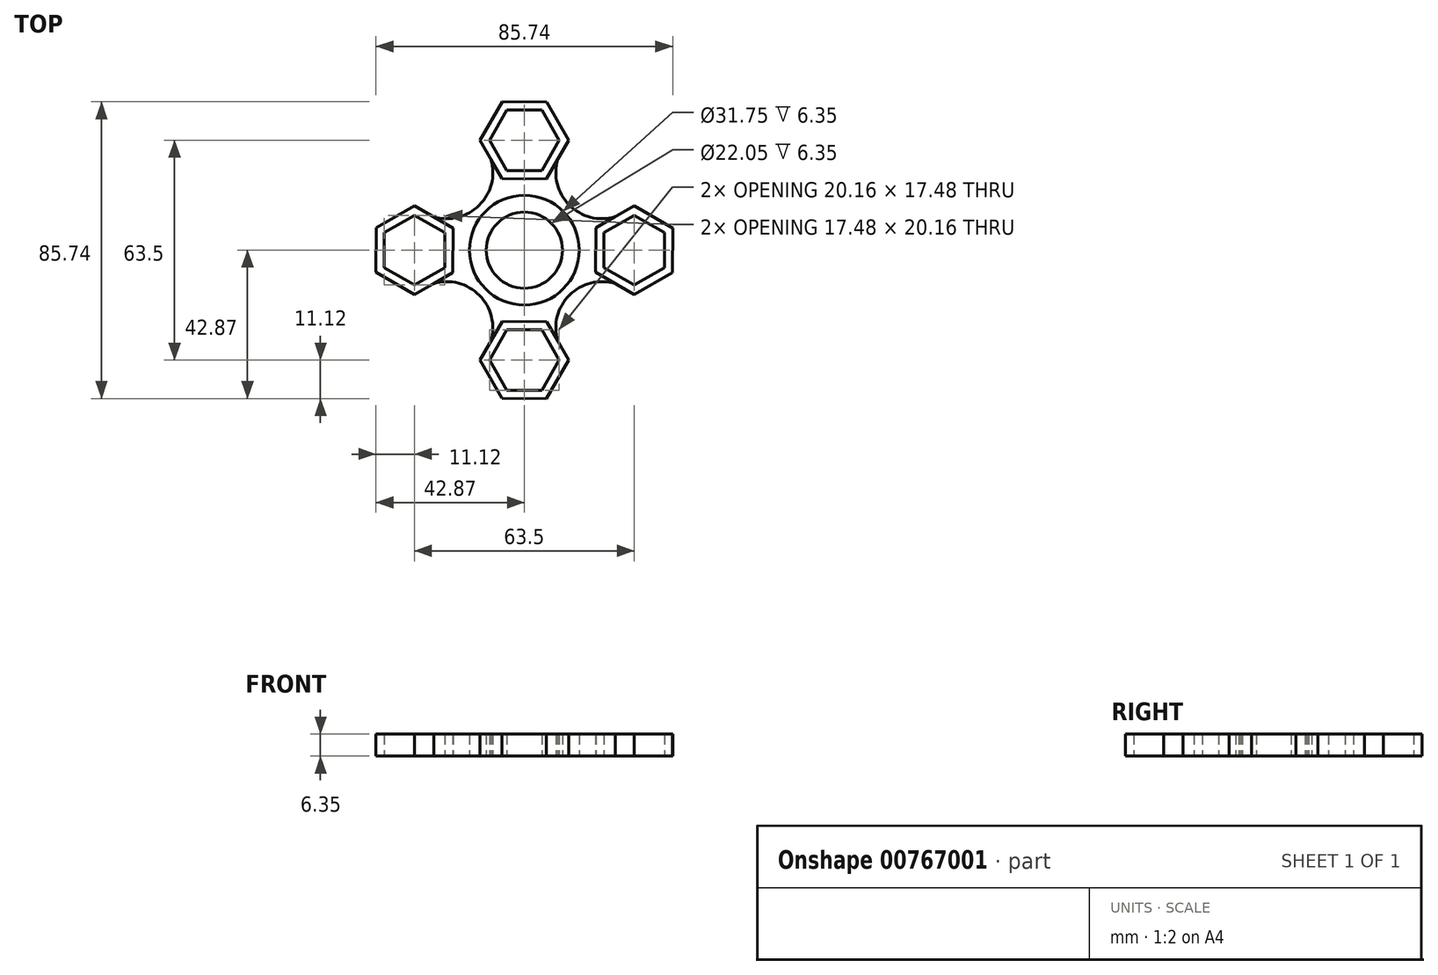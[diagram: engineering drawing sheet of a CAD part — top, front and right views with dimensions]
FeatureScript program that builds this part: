
annotation { "Feature Type Name" : "Feature", "Feature Type Description" : "" }
export const myFeature = defineFeature(function(context is Context, id is Id, definition is map)
    precondition{}
    {
        {
            var Q0;
            Q0=qCreatedBy(makeId("Top.planeOp"),FACE);
            var sketch = newSketch(context, id + "F0", { "sketchPlane" : qUnion([Q0])});
            skCircle(sketch, "E0", {"center": v(0, 0) * mm, "radius": 11.02 * mm});
            skCircle(sketch, "E1", {"center": v(0, 0) * mm, "radius": 15.88 * mm});
            skCircle(sketch, "E2.cCircle", {"center": v(0, 31.75) * mm, "radius": 8.73 * mm, "construction": true});
            skLineSegment(sketch, "E2.0", {"start": v(5.05, 40.47) * mm, "end": v(10.08, 31.73) * mm});
            skLineSegment(sketch, "E2.1", {"start": v(10.08, 31.73) * mm, "end": v(5.03, 23.01) * mm});
            skLineSegment(sketch, "E2.2", {"start": v(5.03, 23.01) * mm, "end": v(-5.05, 23.03) * mm});
            skLineSegment(sketch, "E2.3", {"start": v(-5.05, 23.03) * mm, "end": v(-10.08, 31.77) * mm});
            skLineSegment(sketch, "E2.4", {"start": v(-10.08, 31.77) * mm, "end": v(-5.03, 40.49) * mm});
            skLineSegment(sketch, "E2.5", {"start": v(-5.03, 40.49) * mm, "end": v(5.05, 40.47) * mm});
            skPoint(sketch, "E2.0.midPoint", {"position": v(7.57, 36.1) * mm});
            skCircle(sketch, "E3.cCircle", {"center": v(0, 31.75) * mm, "radius": 11.11 * mm, "construction": true});
            skLineSegment(sketch, "E3.0", {"start": v(12.83, 31.73) * mm, "end": v(6.4, 20.63) * mm});
            skLineSegment(sketch, "E3.1", {"start": v(6.4, 20.63) * mm, "end": v(-6.43, 20.65) * mm});
            skLineSegment(sketch, "E3.2", {"start": v(-6.43, 20.65) * mm, "end": v(-12.83, 31.77) * mm});
            skLineSegment(sketch, "E3.3", {"start": v(-12.83, 31.77) * mm, "end": v(-6.4, 42.87) * mm});
            skLineSegment(sketch, "E3.4", {"start": v(-6.4, 42.87) * mm, "end": v(6.43, 42.85) * mm});
            skLineSegment(sketch, "E3.5", {"start": v(6.43, 42.85) * mm, "end": v(12.83, 31.73) * mm});
            skPoint(sketch, "E3.0.midPoint", {"position": v(9.62, 26.18) * mm});
            skLineSegment(sketch, "E4.1.0", {"start": v(-23.01, 5.03) * mm, "end": v(-23.03, -5.05) * mm});
            skLineSegment(sketch, "E4.1.1", {"start": v(-20.65, -6.43) * mm, "end": v(-31.77, -12.83) * mm});
            skPoint(sketch, "E4.1.2", {"position": v(-36.1, 7.57) * mm});
            skLineSegment(sketch, "E4.1.3", {"start": v(-40.49, -5.03) * mm, "end": v(-40.47, 5.05) * mm});
            skLineSegment(sketch, "E4.1.4", {"start": v(-42.87, -6.4) * mm, "end": v(-42.85, 6.43) * mm});
            skPoint(sketch, "E4.1.5", {"position": v(-26.18, 9.62) * mm});
            skCircle(sketch, "E4.1.6", {"center": v(-31.75, 0) * mm, "radius": 11.11 * mm, "construction": true});
            skCircle(sketch, "E4.1.7", {"center": v(-31.75, 0) * mm, "radius": 8.73 * mm, "construction": true});
            skLineSegment(sketch, "E4.1.8", {"start": v(-23.03, -5.05) * mm, "end": v(-31.77, -10.08) * mm});
            skLineSegment(sketch, "E4.1.9", {"start": v(-31.77, -12.83) * mm, "end": v(-42.87, -6.4) * mm});
            skLineSegment(sketch, "E4.1.10", {"start": v(-31.77, -10.08) * mm, "end": v(-40.49, -5.03) * mm});
            skLineSegment(sketch, "E4.1.11", {"start": v(-20.63, 6.4) * mm, "end": v(-20.65, -6.43) * mm});
            skLineSegment(sketch, "E4.1.12", {"start": v(-31.73, 12.83) * mm, "end": v(-20.63, 6.4) * mm});
            skLineSegment(sketch, "E4.1.13", {"start": v(-42.85, 6.43) * mm, "end": v(-31.73, 12.83) * mm});
            skLineSegment(sketch, "E4.1.14", {"start": v(-31.73, 10.08) * mm, "end": v(-23.01, 5.03) * mm});
            skLineSegment(sketch, "E4.1.15", {"start": v(-40.47, 5.05) * mm, "end": v(-31.73, 10.08) * mm});
            skLineSegment(sketch, "E4.2.0", {"start": v(-5.03, -23.01) * mm, "end": v(5.05, -23.03) * mm});
            skLineSegment(sketch, "E4.2.1", {"start": v(6.43, -20.65) * mm, "end": v(12.83, -31.77) * mm});
            skPoint(sketch, "E4.2.2", {"position": v(-7.57, -36.1) * mm});
            skLineSegment(sketch, "E4.2.3", {"start": v(5.03, -40.49) * mm, "end": v(-5.05, -40.47) * mm});
            skLineSegment(sketch, "E4.2.4", {"start": v(6.4, -42.87) * mm, "end": v(-6.43, -42.85) * mm});
            skPoint(sketch, "E4.2.5", {"position": v(-9.62, -26.18) * mm});
            skCircle(sketch, "E4.2.6", {"center": v(0, -31.75) * mm, "radius": 11.11 * mm, "construction": true});
            skCircle(sketch, "E4.2.7", {"center": v(0, -31.75) * mm, "radius": 8.73 * mm, "construction": true});
            skLineSegment(sketch, "E4.2.8", {"start": v(5.05, -23.03) * mm, "end": v(10.08, -31.77) * mm});
            skLineSegment(sketch, "E4.2.9", {"start": v(12.83, -31.77) * mm, "end": v(6.4, -42.87) * mm});
            skLineSegment(sketch, "E4.2.10", {"start": v(10.08, -31.77) * mm, "end": v(5.03, -40.49) * mm});
            skLineSegment(sketch, "E4.2.11", {"start": v(-6.4, -20.63) * mm, "end": v(6.43, -20.65) * mm});
            skLineSegment(sketch, "E4.2.12", {"start": v(-12.83, -31.73) * mm, "end": v(-6.4, -20.63) * mm});
            skLineSegment(sketch, "E4.2.13", {"start": v(-6.43, -42.85) * mm, "end": v(-12.83, -31.73) * mm});
            skLineSegment(sketch, "E4.2.14", {"start": v(-10.08, -31.73) * mm, "end": v(-5.03, -23.01) * mm});
            skLineSegment(sketch, "E4.2.15", {"start": v(-5.05, -40.47) * mm, "end": v(-10.08, -31.73) * mm});
            skLineSegment(sketch, "E4.3.0", {"start": v(23.01, -5.03) * mm, "end": v(23.03, 5.05) * mm});
            skLineSegment(sketch, "E4.3.1", {"start": v(20.65, 6.43) * mm, "end": v(31.77, 12.83) * mm});
            skPoint(sketch, "E4.3.2", {"position": v(36.1, -7.57) * mm});
            skLineSegment(sketch, "E4.3.3", {"start": v(40.49, 5.03) * mm, "end": v(40.47, -5.05) * mm});
            skLineSegment(sketch, "E4.3.4", {"start": v(42.87, 6.4) * mm, "end": v(42.85, -6.43) * mm});
            skPoint(sketch, "E4.3.5", {"position": v(26.18, -9.62) * mm});
            skCircle(sketch, "E4.3.6", {"center": v(31.75, 0) * mm, "radius": 11.11 * mm, "construction": true});
            skCircle(sketch, "E4.3.7", {"center": v(31.75, 0) * mm, "radius": 8.73 * mm, "construction": true});
            skLineSegment(sketch, "E4.3.8", {"start": v(23.03, 5.05) * mm, "end": v(31.77, 10.08) * mm});
            skLineSegment(sketch, "E4.3.9", {"start": v(31.77, 12.83) * mm, "end": v(42.87, 6.4) * mm});
            skLineSegment(sketch, "E4.3.10", {"start": v(31.77, 10.08) * mm, "end": v(40.49, 5.03) * mm});
            skLineSegment(sketch, "E4.3.11", {"start": v(20.63, -6.4) * mm, "end": v(20.65, 6.43) * mm});
            skLineSegment(sketch, "E4.3.12", {"start": v(31.73, -12.83) * mm, "end": v(20.63, -6.4) * mm});
            skLineSegment(sketch, "E4.3.13", {"start": v(42.85, -6.43) * mm, "end": v(31.73, -12.83) * mm});
            skLineSegment(sketch, "E4.3.14", {"start": v(31.73, -10.08) * mm, "end": v(23.01, -5.03) * mm});
            skLineSegment(sketch, "E4.3.15", {"start": v(40.47, -5.05) * mm, "end": v(31.73, -10.08) * mm});
            skSolve(sketch);
        }
        {
            var Q0;
            Q0=qCreatedBy(makeId("Top.planeOp"),FACE);
            var sketch = newSketch(context, id + "F1", { "sketchPlane" : qUnion([Q0])});
            skLineSegment(sketch, "E5.0", {"start": v(-5.03, -23.01) * mm, "end": v(5.05, -23.03) * mm});
            skCircle(sketch, "E5.1", {"center": v(-31.75, 0) * mm, "radius": 8.73 * mm});
            skLineSegment(sketch, "E5.2", {"start": v(12.83, -31.77) * mm, "end": v(6.4, -42.87) * mm});
            skLineSegment(sketch, "E5.3", {"start": v(-6.4, -20.63) * mm, "end": v(6.43, -20.65) * mm});
            skLineSegment(sketch, "E5.4", {"start": v(31.77, 10.08) * mm, "end": v(40.49, 5.03) * mm});
            skCircle(sketch, "E5.5", {"center": v(0, 0) * mm, "radius": 15.88 * mm});
            skLineSegment(sketch, "E5.6", {"start": v(5.03, -40.49) * mm, "end": v(-5.05, -40.47) * mm});
            skLineSegment(sketch, "E5.7", {"start": v(-42.87, -6.4) * mm, "end": v(-42.85, 6.43) * mm});
            skLineSegment(sketch, "E5.8", {"start": v(20.63, -6.4) * mm, "end": v(20.65, 6.43) * mm});
            skCircle(sketch, "E5.9", {"center": v(0, 0) * mm, "radius": 11.02 * mm});
            skLineSegment(sketch, "E5.10", {"start": v(-6.4, 42.87) * mm, "end": v(6.43, 42.85) * mm});
            skLineSegment(sketch, "E5.11", {"start": v(-40.49, -5.03) * mm, "end": v(-40.47, 5.05) * mm});
            skLineSegment(sketch, "E5.12", {"start": v(10.08, -31.77) * mm, "end": v(5.03, -40.49) * mm});
            skLineSegment(sketch, "E5.13", {"start": v(42.87, 6.4) * mm, "end": v(42.85, -6.43) * mm});
            skLineSegment(sketch, "E5.14", {"start": v(-20.63, 6.4) * mm, "end": v(-20.65, -6.43) * mm});
            skLineSegment(sketch, "E5.15", {"start": v(-23.01, 5.03) * mm, "end": v(-23.03, -5.05) * mm});
            skLineSegment(sketch, "E5.16", {"start": v(-6.43, -42.85) * mm, "end": v(-12.83, -31.73) * mm});
            skLineSegment(sketch, "E5.17", {"start": v(5.03, 23.01) * mm, "end": v(-5.05, 23.03) * mm});
            skLineSegment(sketch, "E5.18", {"start": v(-5.03, 40.49) * mm, "end": v(5.05, 40.47) * mm});
            skLineSegment(sketch, "E5.19", {"start": v(-6.43, 20.65) * mm, "end": v(-12.83, 31.77) * mm});
            skLineSegment(sketch, "E5.20", {"start": v(5.05, -23.03) * mm, "end": v(10.08, -31.77) * mm});
            skLineSegment(sketch, "E5.21", {"start": v(31.77, 12.83) * mm, "end": v(42.87, 6.4) * mm});
            skLineSegment(sketch, "E5.22", {"start": v(-5.05, 23.03) * mm, "end": v(-10.08, 31.77) * mm});
            skLineSegment(sketch, "E5.23", {"start": v(-31.77, -10.08) * mm, "end": v(-40.49, -5.03) * mm});
            skCircle(sketch, "E5.24", {"center": v(0, 31.75) * mm, "radius": 8.73 * mm});
            skLineSegment(sketch, "E5.25", {"start": v(23.01, -5.03) * mm, "end": v(23.03, 5.05) * mm});
            skLineSegment(sketch, "E5.26", {"start": v(40.49, 5.03) * mm, "end": v(40.47, -5.05) * mm});
            skLineSegment(sketch, "E5.27", {"start": v(-10.08, 31.77) * mm, "end": v(-5.03, 40.49) * mm});
            skLineSegment(sketch, "E5.28", {"start": v(6.4, 20.63) * mm, "end": v(-6.43, 20.65) * mm});
            skCircle(sketch, "E5.29", {"center": v(0, -31.75) * mm, "radius": 8.73 * mm});
            skLineSegment(sketch, "E5.30", {"start": v(-12.83, 31.77) * mm, "end": v(-6.4, 42.87) * mm});
            skLineSegment(sketch, "E5.31", {"start": v(-31.77, -12.83) * mm, "end": v(-42.87, -6.4) * mm});
            skLineSegment(sketch, "E5.32", {"start": v(-20.65, -6.43) * mm, "end": v(-31.77, -12.83) * mm});
            skLineSegment(sketch, "E5.33", {"start": v(-23.03, -5.05) * mm, "end": v(-31.77, -10.08) * mm});
            skLineSegment(sketch, "E5.34", {"start": v(6.43, -20.65) * mm, "end": v(12.83, -31.77) * mm});
            skLineSegment(sketch, "E5.35", {"start": v(20.65, 6.43) * mm, "end": v(31.77, 12.83) * mm});
            skCircle(sketch, "E5.36", {"center": v(31.75, 0) * mm, "radius": 8.73 * mm});
            skLineSegment(sketch, "E5.37", {"start": v(6.4, -42.87) * mm, "end": v(-6.43, -42.85) * mm});
            skLineSegment(sketch, "E5.38", {"start": v(23.03, 5.05) * mm, "end": v(31.77, 10.08) * mm});
            skCircle(sketch, "E5.39", {"center": v(0, -31.75) * mm, "radius": 11.11 * mm});
            skCircle(sketch, "E5.40", {"center": v(-31.75, 0) * mm, "radius": 11.11 * mm});
            skLineSegment(sketch, "E5.41", {"start": v(31.73, -10.08) * mm, "end": v(23.01, -5.03) * mm});
            skLineSegment(sketch, "E5.42", {"start": v(42.85, -6.43) * mm, "end": v(31.73, -12.83) * mm});
            skLineSegment(sketch, "E5.43", {"start": v(-31.73, 10.08) * mm, "end": v(-23.01, 5.03) * mm});
            skCircle(sketch, "E5.44", {"center": v(0, 31.75) * mm, "radius": 11.11 * mm});
            skLineSegment(sketch, "E5.45", {"start": v(12.83, 31.73) * mm, "end": v(6.4, 20.63) * mm});
            skLineSegment(sketch, "E5.46", {"start": v(-42.85, 6.43) * mm, "end": v(-31.73, 12.83) * mm});
            skCircle(sketch, "E5.47", {"center": v(31.75, 0) * mm, "radius": 11.11 * mm});
            skLineSegment(sketch, "E6.0", {"start": v(-31.73, 12.83) * mm, "end": v(-20.63, 6.4) * mm});
            skLineSegment(sketch, "E7.0", {"start": v(-12.83, -31.73) * mm, "end": v(-6.4, -20.63) * mm});
            skLineSegment(sketch, "E8.0", {"start": v(-10.08, -31.73) * mm, "end": v(-5.03, -23.01) * mm});
            skLineSegment(sketch, "E9.0", {"start": v(-5.05, -40.47) * mm, "end": v(-10.08, -31.73) * mm});
            skLineSegment(sketch, "E10.0", {"start": v(31.73, -12.83) * mm, "end": v(20.63, -6.4) * mm});
            skPoint(sketch, "E11.0", {"position": v(10.08, 31.73) * mm});
            skLineSegment(sketch, "E12.0", {"start": v(5.05, 40.47) * mm, "end": v(10.08, 31.73) * mm});
            skLineSegment(sketch, "E13.0", {"start": v(6.43, 42.85) * mm, "end": v(12.83, 31.73) * mm});
            skLineSegment(sketch, "E14.0", {"start": v(10.08, 31.73) * mm, "end": v(5.03, 23.01) * mm});
            skArc(sketch, "E15", {"start": v(-31.73, 12.83) * mm, "mid": v(-13, 13.04) * mm, "end": v(-12.83, 31.77) * mm});
            skArc(sketch, "E16", {"start": v(31.73, -12.83) * mm, "mid": v(13, -13.04) * mm, "end": v(12.83, -31.77) * mm});
            skArc(sketch, "E17", {"start": v(-12.83, -31.73) * mm, "mid": v(-13.04, -13) * mm, "end": v(-31.77, -12.83) * mm});
            skArc(sketch, "E18", {"start": v(12.83, 31.73) * mm, "mid": v(13.04, 13) * mm, "end": v(31.77, 12.83) * mm});
            skSolve(sketch);
        }
        {
            var Q0;
            Q0=makeQuery(id+"F1.imprint","IMPRINT",FACE,{"disambiguationData":[TD([[makeQuery(id+"F1.imprint","IMPRINT",EDGE,{"derivedFrom":sQuery(id+"F1.wireOp",EDGE,"E5.5")}),-1.0]])]});
            var Q1;
            Q1=makeQuery(id+"F0.imprint","IMPRINT",FACE,{"disambiguationData":[TD([[makeQuery(id+"F0.imprint","IMPRINT",EDGE,{"derivedFrom":sQuery(id+"F0.wireOp",EDGE,"E0")}),-1.0]])]});
            var Q2;
            Q2=makeQuery(id+"F0.imprint","IMPRINT",FACE,{"disambiguationData":[TD([[makeQuery(id+"F0.imprint","IMPRINT",EDGE,{"derivedFrom":sQuery(id+"F0.wireOp",EDGE,"E2.0")}),1.0]])]});
            var Q3;
            Q3=makeQuery(id+"F0.imprint","IMPRINT",FACE,{"disambiguationData":[TD([[makeQuery(id+"F0.imprint","IMPRINT",EDGE,{"derivedFrom":sQuery(id+"F0.wireOp",EDGE,"E4.3.0")}),1.0]])]});
            var Q4;
            Q4=makeQuery(id+"F0.imprint","IMPRINT",FACE,{"disambiguationData":[TD([[makeQuery(id+"F0.imprint","IMPRINT",EDGE,{"derivedFrom":sQuery(id+"F0.wireOp",EDGE,"E4.2.0")}),1.0]])]});
            var Q5;
            Q5=makeQuery(id+"F0.imprint","IMPRINT",FACE,{"disambiguationData":[TD([[makeQuery(id+"F0.imprint","IMPRINT",EDGE,{"derivedFrom":sQuery(id+"F0.wireOp",EDGE,"E4.1.0")}),1.0]])]});
            extrude(context, id + "F2", {"entities" : qUnion([Q0, Q1, Q2, Q3, Q4, Q5]), "depth" : 6.35 * mm, "offsetDistance" : 25.4 * mm});
        }
    });
